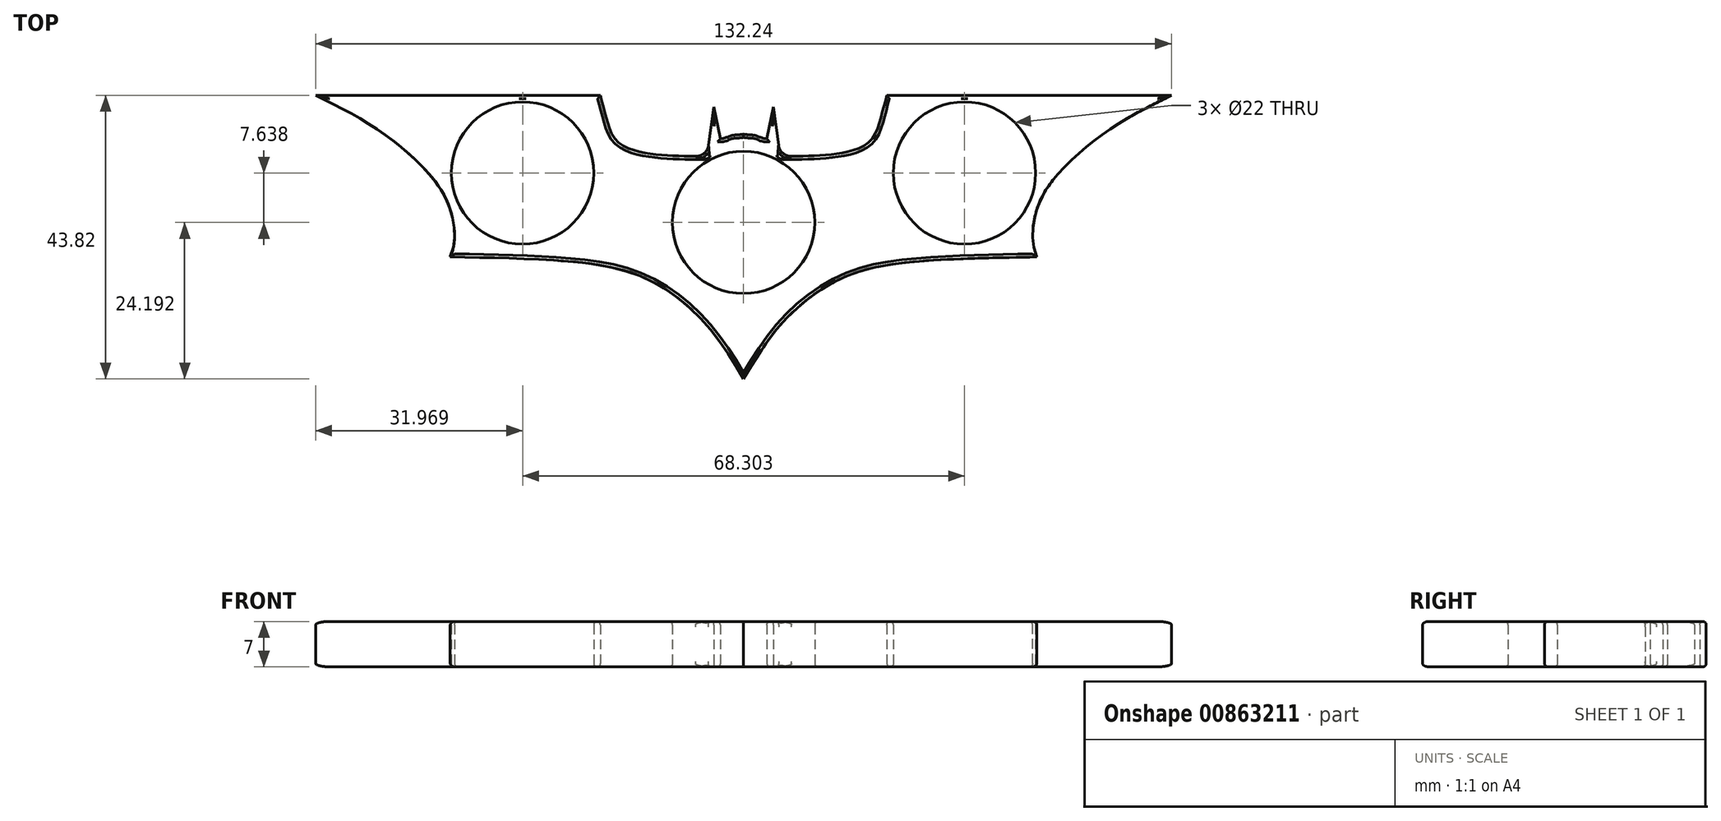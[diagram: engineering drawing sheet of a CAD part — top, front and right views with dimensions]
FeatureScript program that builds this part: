
annotation { "Feature Type Name" : "Feature", "Feature Type Description" : "" }
export const myFeature = defineFeature(function(context is Context, id is Id, definition is map)
    precondition{}
    {
        {
            var Q0;
            Q0=qCreatedBy(makeId("Top.planeOp"),FACE);
            var sketch = newSketch(context, id + "F0", { "sketchPlane" : qUnion([Q0])});
            skCircle(sketch, "E0", {"center": v(34.15, 3) * mm, "radius": 11 * mm});
            skCircle(sketch, "E1", {"center": v(0, -4.64) * mm, "radius": 11 * mm});
            skFitSpline(sketch, "E2", {"points": [v(66.12, 14.99) * mm, v(56.4, 9.6) * mm, v(47.88, 1.98) * mm, v(45.03, -3.7) * mm, v(45.33, -9.99) * mm], "startDerivative": vector(-34.46, -16.89) * mm, "endDerivative": vector(12.6, -27.31) * mm});
            skFitSpline(sketch, "E3", {"points": [v(0, -28.83) * mm, v(5.85, -20.3) * mm, v(14.82, -13.43) * mm, v(26.2, -10.73) * mm, v(45.33, -9.99) * mm], "startDerivative": vector(23.38, 39.27) * mm, "endDerivative": vector(66.84, 1.08) * mm});
            skLineSegment(sketch, "E4", {"start": v(66.12, 14.99) * mm, "end": v(22.15, 14.99) * mm});
            skFitSpline(sketch, "E5", {"points": [v(22.15, 14.99) * mm, v(21.12, 11.16) * mm, v(19.74, 8.13) * mm, v(15.72, 6.2) * mm, v(5.65, 5.55) * mm], "startDerivative": vector(-4.7, -17.78) * mm, "endDerivative": vector(-31.64, -0.41) * mm});
            skLineSegment(sketch, "E6", {"start": v(4.6, 13.2) * mm, "end": v(5.65, 5.55) * mm});
            skLineSegment(sketch, "E7", {"start": v(4.6, 13.2) * mm, "end": v(3.6, 8.3) * mm});
            skFitSpline(sketch, "E8", {"points": [v(3.6, 8.3) * mm, v(1.9, 8.78) * mm, v(0, 9.01) * mm], "startDerivative": vector(-4.72, 0) * mm, "endDerivative": vector(-3.6, 0.88) * mm});
            skFitSpline(sketch, "E9.MirrorCS", {"points": [v(-3.6, 8.3) * mm, v(-1.9, 8.78) * mm, v(0, 9.01) * mm], "startDerivative": vector(4.72, 0) * mm, "endDerivative": vector(3.6, 0.88) * mm});
            skLineSegment(sketch, "E10.MirrorCS", {"start": v(-4.6, 13.2) * mm, "end": v(-3.6, 8.3) * mm});
            skLineSegment(sketch, "E11.MirrorCS", {"start": v(-66.12, 14.99) * mm, "end": v(-22.15, 14.99) * mm});
            skLineSegment(sketch, "E12.MirrorCS", {"start": v(-4.6, 13.2) * mm, "end": v(-5.65, 5.55) * mm});
            skFitSpline(sketch, "E13.MirrorCS", {"points": [v(-22.15, 14.99) * mm, v(-21.12, 11.16) * mm, v(-19.74, 8.13) * mm, v(-15.72, 6.2) * mm, v(-5.65, 5.55) * mm], "startDerivative": vector(4.7, -17.78) * mm, "endDerivative": vector(31.64, -0.41) * mm});
            skCircle(sketch, "E14.MirrorC", {"center": v(-34.15, 3) * mm, "radius": 11 * mm});
            skFitSpline(sketch, "E15.MirrorCS", {"points": [v(-66.12, 14.99) * mm, v(-56.4, 9.6) * mm, v(-47.88, 1.98) * mm, v(-45.03, -3.7) * mm, v(-45.33, -9.99) * mm], "startDerivative": vector(34.46, -16.89) * mm, "endDerivative": vector(-12.6, -27.31) * mm});
            skFitSpline(sketch, "E16.MirrorCS", {"points": [v(0, -28.83) * mm, v(-5.85, -20.3) * mm, v(-14.82, -13.43) * mm, v(-26.2, -10.73) * mm, v(-45.33, -9.99) * mm], "startDerivative": vector(-23.38, 39.27) * mm, "endDerivative": vector(-66.84, 1.08) * mm});
            skSolve(sketch);
        }
        {
            var Q0;
            Q0=makeQuery(id+"F0.imprint","IMPRINT",FACE,{"disambiguationData":[TD([[makeQuery(id+"F0.imprint","IMPRINT",EDGE,{"derivedFrom":sQuery(id+"F0.wireOp",EDGE,"E0")}),-1.0]])]});
            extrude(context, id + "F1", {"entities" : qUnion([Q0]), "depth" : 7 * mm, "offsetDistance" : 25 * mm});
        }
        {
            var Q0;
            Q0=makeQuery(id+"F1.opExtrude","CAP_FACE",FACE,{"disambiguationData":[OSD([sQuery(id+"F0.wireOp",EDGE,"E0"),sQuery(id+"F0.wireOp",EDGE,"E2"),sQuery(id+"F0.wireOp",EDGE,"E3"),sQuery(id+"F0.wireOp",EDGE,"E4"),sQuery(id+"F0.wireOp",EDGE,"E5"),sQuery(id+"F0.wireOp",EDGE,"E6"),sQuery(id+"F0.wireOp",EDGE,"E7"),sQuery(id+"F0.wireOp",EDGE,"E8"),sQuery(id+"F0.wireOp",EDGE,"E9.MirrorCS"),sQuery(id+"F0.wireOp",EDGE,"E10.MirrorCS"),sQuery(id+"F0.wireOp",EDGE,"E11.MirrorCS"),sQuery(id+"F0.wireOp",EDGE,"E12.MirrorCS"),sQuery(id+"F0.wireOp",EDGE,"E13.MirrorCS"),sQuery(id+"F0.wireOp",EDGE,"E14.MirrorC"),sQuery(id+"F0.wireOp",EDGE,"E15.MirrorCS"),sQuery(id+"F0.wireOp",EDGE,"E16.MirrorCS"),sQuery(id+"F0.wireOp",EDGE,"E1")])],"isStart":false});
            fillet(context, id + "F2", {"entities" : qUnion([Q0]), "radius" : .5 * mm, "tangentPropagation" : true, "allowEdgeOverflow" : false});
        }
        {
            var Q0;
            Q0=makeQuery(id+"F1.opExtrude","CAP_FACE",FACE,{"disambiguationData":[OSD([sQuery(id+"F0.wireOp",EDGE,"E0"),sQuery(id+"F0.wireOp",EDGE,"E2"),sQuery(id+"F0.wireOp",EDGE,"E3"),sQuery(id+"F0.wireOp",EDGE,"E4"),sQuery(id+"F0.wireOp",EDGE,"E5"),sQuery(id+"F0.wireOp",EDGE,"E6"),sQuery(id+"F0.wireOp",EDGE,"E7"),sQuery(id+"F0.wireOp",EDGE,"E8"),sQuery(id+"F0.wireOp",EDGE,"E9.MirrorCS"),sQuery(id+"F0.wireOp",EDGE,"E10.MirrorCS"),sQuery(id+"F0.wireOp",EDGE,"E11.MirrorCS"),sQuery(id+"F0.wireOp",EDGE,"E12.MirrorCS"),sQuery(id+"F0.wireOp",EDGE,"E13.MirrorCS"),sQuery(id+"F0.wireOp",EDGE,"E14.MirrorC"),sQuery(id+"F0.wireOp",EDGE,"E15.MirrorCS"),sQuery(id+"F0.wireOp",EDGE,"E16.MirrorCS"),sQuery(id+"F0.wireOp",EDGE,"E1")])],"isStart":true});
            fillet(context, id + "F3", {"entities" : qUnion([Q0]), "radius" : .5 * mm, "tangentPropagation" : true, "allowEdgeOverflow" : false});
        }
        {
            var Q0;
            Q0=makeQuery(id+"F1.opExtrude","SWEPT_EDGE",EDGE,{"disambiguationData":[OSD([sQuery(id+"F0.wireOp",EDGE,"E5"),sQuery(id+"F0.wireOp",EDGE,"E6")])]});
            var Q1;
            Q1=makeQuery(id+"F1.opExtrude","SWEPT_EDGE",EDGE,{"disambiguationData":[OSD([sQuery(id+"F0.wireOp",EDGE,"E12.MirrorCS"),sQuery(id+"F0.wireOp",EDGE,"E13.MirrorCS")])]});
            fillet(context, id + "F4", {"entities" : qUnion([Q0, Q1]), "radius" : 2 * mm, "tangentPropagation" : true, "allowEdgeOverflow" : false});
        }
    });
